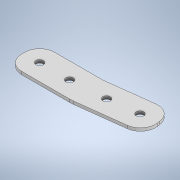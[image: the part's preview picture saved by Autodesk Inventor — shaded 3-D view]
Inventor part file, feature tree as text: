
AUTODESK INVENTOR PART (.ipt)
format: ipt  version: 2021 (Build 250183000, 183)  size: 138,752 bytes
history: native  units: mm
features: extrude x1, sketch x1
ambient origin geometry x8: Origin, YZ Plane, XZ Plane, XY Plane, X Axis, Y Axis, Z Axis, Center Point
bodies: Solid1 (feature_tree)
feature tree (2):
  extrude  "Extrusion1"  Depth=10.0mm
  sketch  "Sketch1"  dims[d0=42.0mm d3=16.929694mm d4=42.0mm d5=11.0mm d6=20.0mm d7=22.0mm d8=11.0mm d9=11.0mm d10=5.0mm d11=5.0mm d12=11.0mm d13=11.0mm d14=90.0deg d15=20.0mm d16=5.0mm d17=5.0mm d18=2.0mm d19=0.0mm d20=10.0mm d21=10.0mm]
